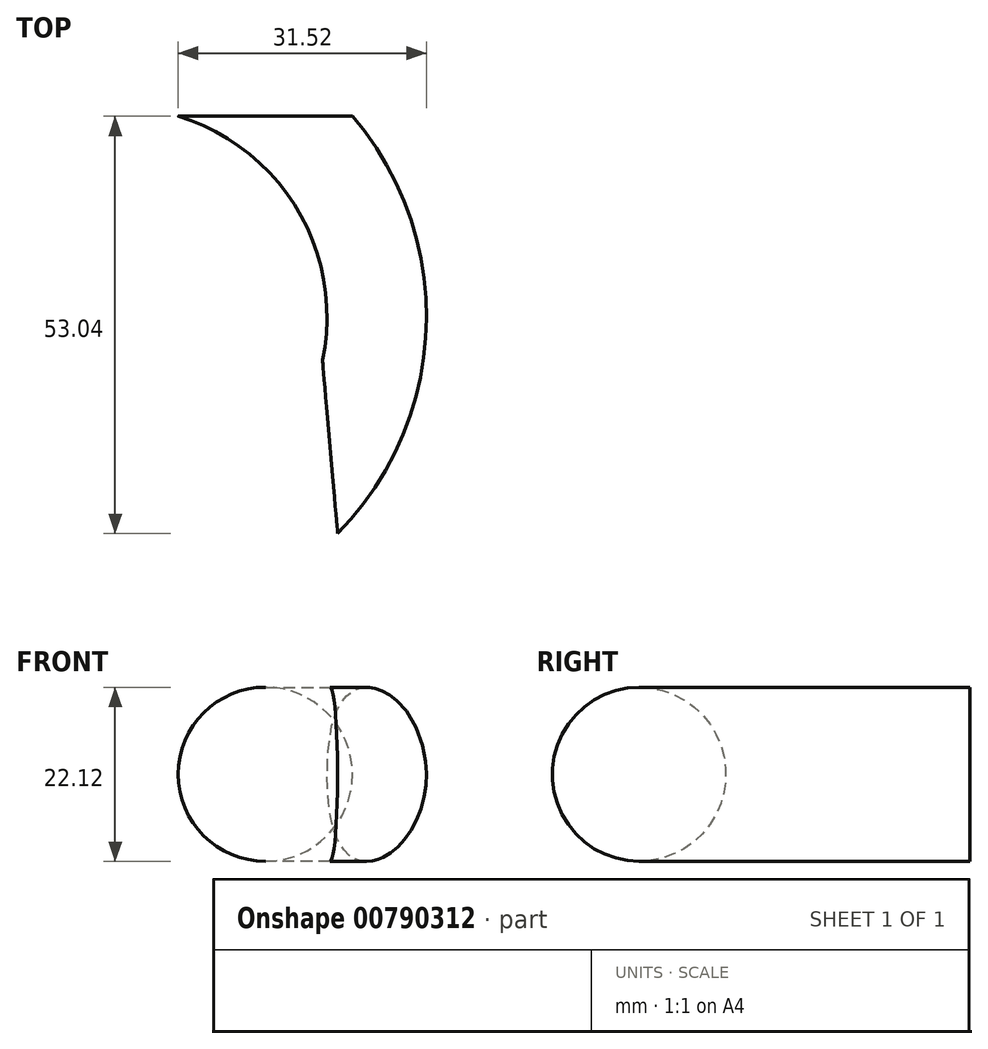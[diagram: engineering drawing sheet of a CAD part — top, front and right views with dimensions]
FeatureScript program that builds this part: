
annotation { "Feature Type Name" : "Feature", "Feature Type Description" : "" }
export const myFeature = defineFeature(function(context is Context, id is Id, definition is map)
    precondition{}
    {
        {
            var Q0;
            Q0=qCreatedBy(makeId("Front.planeOp"),FACE);
            var sketch = newSketch(context, id + "F0", { "sketchPlane" : qUnion([Q0])});
            skCircle(sketch, "E0", {"center": v(0, 0) * mm, "radius": 11.06 * mm});
            skSolve(sketch);
        }
        {
            var Q0;
            Q0=qCreatedBy(makeId("Top.planeOp"),FACE);
            var sketch = newSketch(context, id + "F1", { "sketchPlane" : qUnion([Q0])});
            skArc(sketch, "E1", {"start": v(8.22, -42.02) * mm, "mid": v(12.28, -19.41) * mm, "end": v(0, 0) * mm});
            skSolve(sketch);
        }
        {
            var Q0;
            Q0 = qSketchRegion(id + "F0", true);
            var Q1;
            Q1 = qConstructionFilter(qBodyType(qCreatedBy(id + "F1" ,EDGE), BodyType.WIRE), ConstructionObject.NO);
            sweep(context, id + "F2", {"profiles" : qUnion([Q0]), "path" : qUnion([Q1])});
        }
    });
